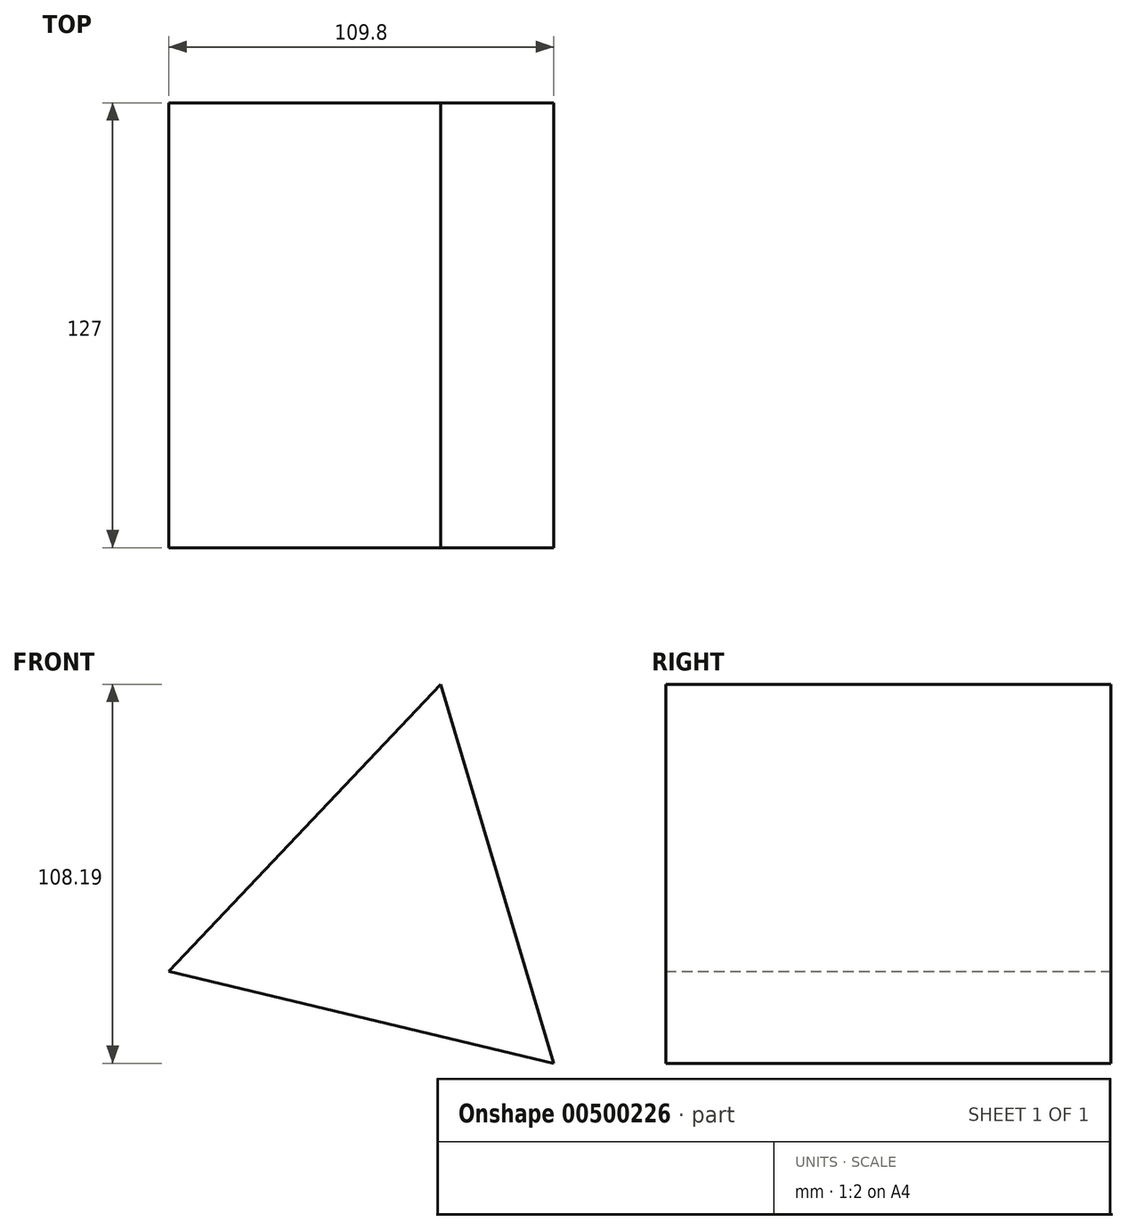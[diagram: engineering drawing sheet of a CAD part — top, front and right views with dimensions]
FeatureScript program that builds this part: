
annotation { "Feature Type Name" : "Feature", "Feature Type Description" : "" }
export const myFeature = defineFeature(function(context is Context, id is Id, definition is map)
    precondition{}
    {
        {
            var Q0;
            Q0=qCreatedBy(makeId("Front.planeOp"),FACE);
            var sketch = newSketch(context, id + "F0", { "sketchPlane" : qUnion([Q0])});
            skCircle(sketch, "E0.cCircle", {"center": v(0.03, -0.29) * mm, "radius": 65.17 * mm, "construction": true});
            skLineSegment(sketch, "E0.0", {"start": v(47.36, -45.09) * mm, "end": v(-62.44, -18.88) * mm});
            skLineSegment(sketch, "E0.1", {"start": v(-62.44, -18.88) * mm, "end": v(15.16, 63.1) * mm});
            skLineSegment(sketch, "E0.2", {"start": v(15.16, 63.1) * mm, "end": v(47.36, -45.09) * mm});
            skSolve(sketch);
        }
        {
            var Q0;
            Q0 = qSketchRegion(id + "F0", true);
            extrude(context, id + "F1", {"entities" : qUnion([Q0]), "depth" : 127 * mm});
        }
    });
